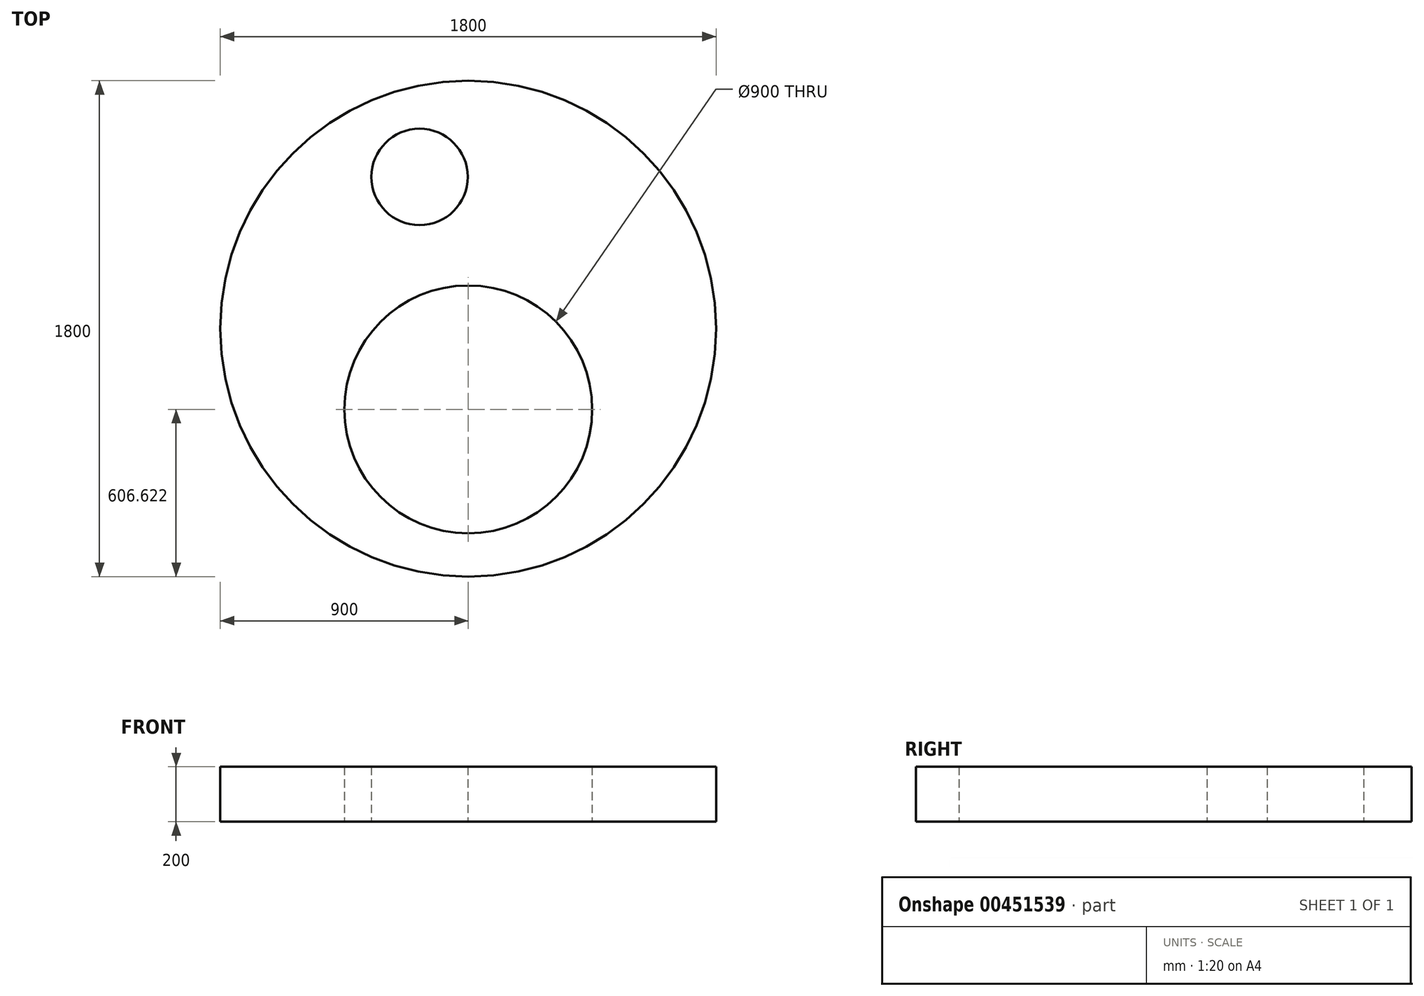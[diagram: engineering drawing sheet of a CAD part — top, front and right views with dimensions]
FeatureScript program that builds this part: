
annotation { "Feature Type Name" : "Feature", "Feature Type Description" : "" }
export const myFeature = defineFeature(function(context is Context, id is Id, definition is map)
    precondition{}
    {
        {
            var Q0;
            Q0=qCreatedBy(makeId("Top.planeOp"),FACE);
            var sketch = newSketch(context, id + "F0", { "sketchPlane" : qUnion([Q0])});
            skCircle(sketch, "E0", {"center": v(0, 0) * mm, "radius": 900 * mm});
            skCircle(sketch, "E1", {"center": v(0, -293.38) * mm, "radius": 450 * mm});
            skCircle(sketch, "E2", {"center": v(-176.75, 550.72) * mm, "radius": 175 * mm});
            skSolve(sketch);
        }
        {
            var Q0;
            Q0=makeQuery(id+"F0.imprint","IMPRINT",FACE,{"disambiguationData":[TD([[makeQuery(id+"F0.imprint","IMPRINT",EDGE,{"derivedFrom":sQuery(id+"F0.wireOp",EDGE,"E0")}),1.0]])]});
            extrude(context, id + "F1", {"entities" : qUnion([Q0]), "endBound" : BoundingType.SYMMETRIC, "depth" : 200 * mm});
        }
    });
